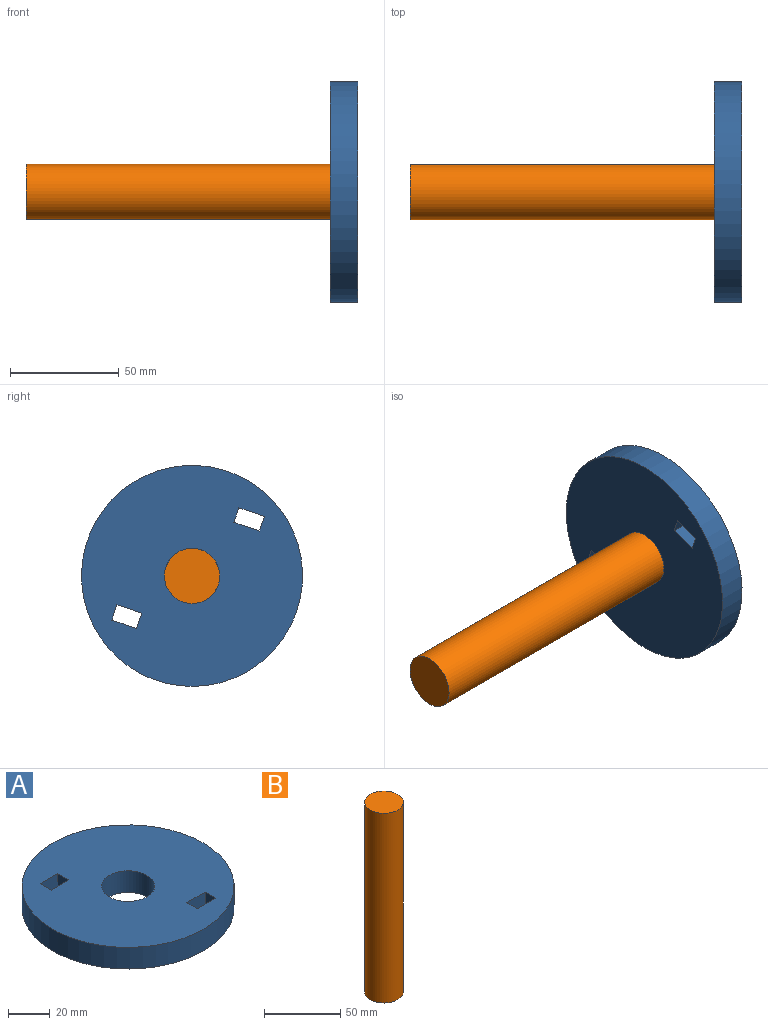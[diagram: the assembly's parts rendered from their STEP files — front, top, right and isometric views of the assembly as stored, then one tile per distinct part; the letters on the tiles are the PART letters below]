
ASSEMBLY  parts=2 mates=1
PART A: 12 faces, bbox 101.6x101.6x12.7 mm
  f0: plane 12.7x12.42mm, normal (0,1,0), area 157.7mm2, adj f1,f7,f10,f11
  f1: plane 12.7x7.09mm, normal (1,0,0), area 90.1mm2, adj f0,f2,f10,f11
  f2: plane 12.7x12.42mm, normal (0,-1,0), area 157.7mm2, adj f1,f7,f10,f11
  f3: plane 12.7x12.02mm, normal (0,1,0), area 152.7mm2, adj f4,f8,f10,f11
  f4: plane 12.7x7.49mm, normal (1,0,0), area 95.1mm2, adj f3,f5,f10,f11
  f5: plane 12.7x12.02mm, normal (0,-1,0), area 152.7mm2, adj f4,f8,f10,f11
  f6: cylinder r=12.7mm len=25.4mm, axis (0,0,-1), area 1013.4mm2, adj f10,f11
  f7: plane 12.7x7.09mm, normal (-1,0,0), area 90.1mm2, adj f0,f2,f10,f11
  f8: plane 12.7x7.49mm, normal (-1,0,0), area 95.1mm2, adj f3,f5,f10,f11
  f9: cylinder r=50.8mm len=101.6mm, axis (0,0,-1), area 4053.7mm2, adj f10,f11
  f10: plane 101.6x101.6mm, normal (0,0,1), area 7422.5mm2, adj f0,f1,f2,f3,f4,f5,f6,f7
  f11: plane 101.6x101.6mm, normal (0,0,-1), area 7422.5mm2, adj f0,f1,f2,f3,f4,f5,f6,f7
PART B: 3 faces, bbox 25.4x25.4x152.4 mm
  f0: cylinder r=12.7mm len=152.4mm, axis (0,0,-1), area 12161mm2, adj f1,f2
  f1: plane 25.4x25.4mm, normal (0,0,1), area 506.7mm2, adj f0
  f2: plane 25.4x25.4mm, normal (0,0,-1), area 506.7mm2, adj f0
PLACE A rot(axis=(-0.5,0.7,-0.5),109.8deg) t=(64.12,-3.12,32.39)mm
PLACE B rot(axis=(0,1,0),90deg) t=(-5.73,-3.12,32.39)mm fixed
MATE revolute B.f0 <-> A.f6  axis (1,0,0) through (70.47,-3.12,32.39)mm
